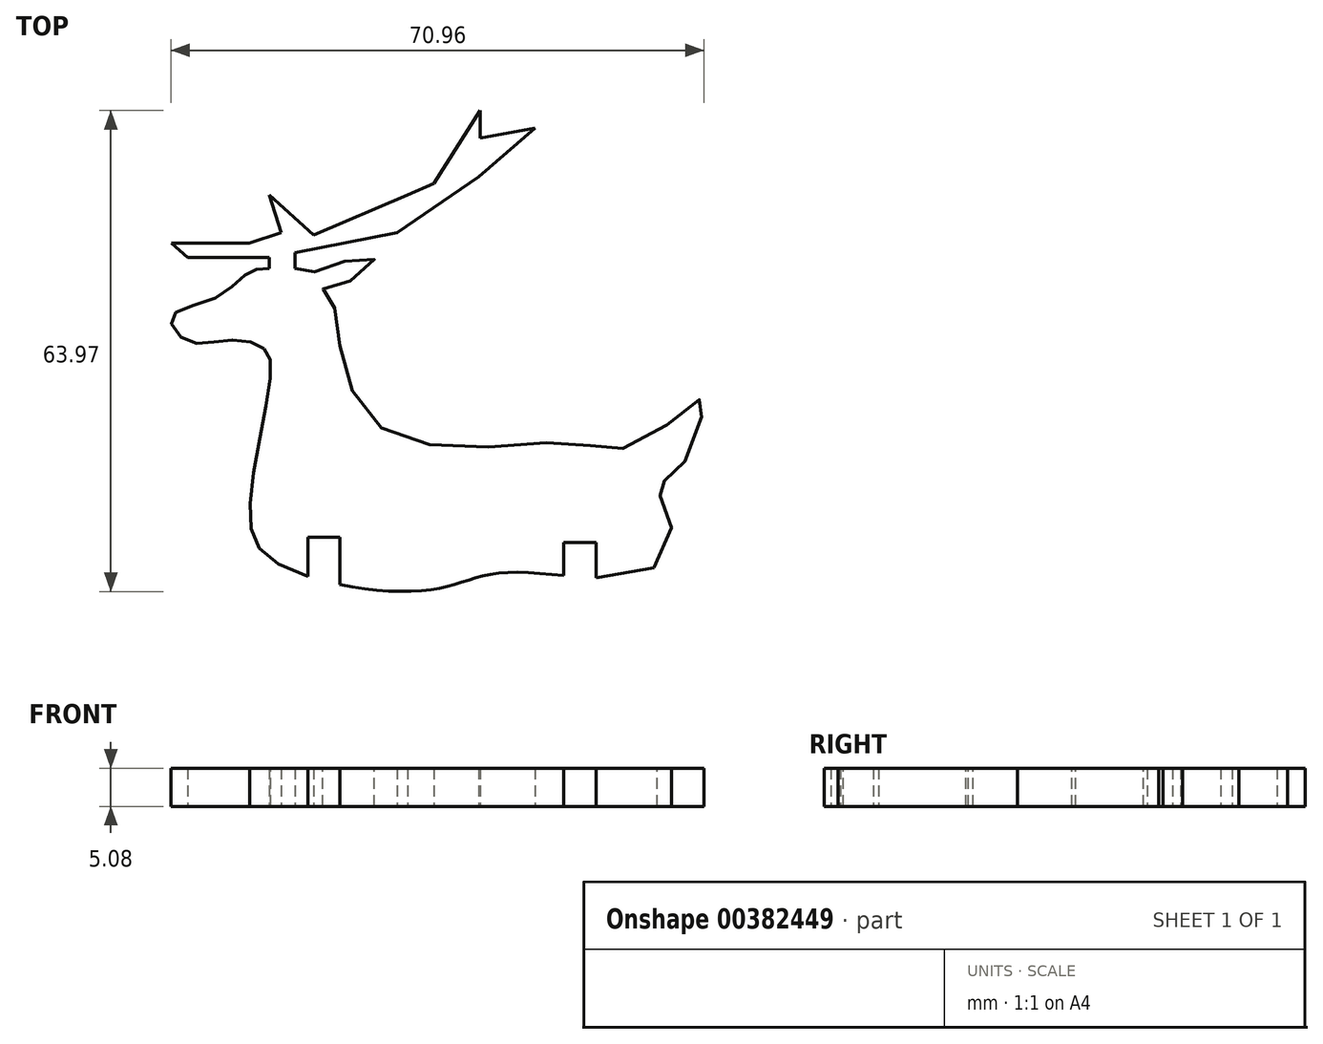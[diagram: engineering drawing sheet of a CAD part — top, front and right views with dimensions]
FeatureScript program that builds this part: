
annotation { "Feature Type Name" : "Feature", "Feature Type Description" : "" }
export const myFeature = defineFeature(function(context is Context, id is Id, definition is map)
    precondition{}
    {
        {
            var Q0;
            Q0=qCreatedBy(makeId("Top.planeOp"),FACE);
            var sketch = newSketch(context, id + "F0", { "sketchPlane" : qUnion([Q0])});
            skFitSpline(sketch, "E0", {"points": [v(-34.96, 24.7) * mm, v(-37.12, 27.92) * mm, v(-31.22, 30.47) * mm, v(-26.8, 33.87) * mm, v(-24.1, 34.38) * mm, v(-20.7, 34.38) * mm, v(-18.66, 33.87) * mm, v(-15.94, 34.72) * mm, v(-10.17, 35.74) * mm, v(-13.4, 32.68) * mm, v(-16.96, 31.66) * mm, v(-15.77, 29.96) * mm, v(-14.58, 23.34) * mm, v(-10, 13.83) * mm, v(3.08, 10.6) * mm, v(17.34, 11.11) * mm, v(22.78, 10.43) * mm, v(32.29, 16.2) * mm, v(33.7, 17.06) * mm, v(31.6, 9.42) * mm, v(28.55, 6.19) * mm, v(27.53, 5) * mm, v(28.89, 2.62) * mm, v(27.2, -5.36) * mm, v(7.5, -6.04) * mm, v(-3.03, -8.41) * mm, v(-23.58, -4.5) * mm, v(-26.64, 3.64) * mm, v(-23.92, 20.45) * mm, v(-24.94, 23.85) * mm, v(-29.7, 24.87) * mm, v(-34.96, 24.7) * mm]});
            skLineSegment(sketch, "E1", {"start": v(-24.1, 34.38) * mm, "end": v(-24.1, 35.84) * mm});
            skLineSegment(sketch, "E2", {"start": v(-24.1, 35.84) * mm, "end": v(-34.96, 35.84) * mm});
            skLineSegment(sketch, "E3", {"start": v(-34.96, 35.84) * mm, "end": v(-37.12, 37.77) * mm});
            skLineSegment(sketch, "E4", {"start": v(-37.12, 37.77) * mm, "end": v(-26.8, 37.77) * mm});
            skLineSegment(sketch, "E5", {"start": v(-26.8, 37.77) * mm, "end": v(-22.5, 39.15) * mm});
            skLineSegment(sketch, "E6", {"start": v(-22.5, 39.15) * mm, "end": v(-24.1, 44.16) * mm});
            skLineSegment(sketch, "E7", {"start": v(-24.1, 44.16) * mm, "end": v(-21.57, 41.9) * mm});
            skLineSegment(sketch, "E8", {"start": v(-21.57, 41.9) * mm, "end": v(-18.17, 38.86) * mm});
            skLineSegment(sketch, "E9", {"start": v(-18.17, 38.86) * mm, "end": v(-5.67, 44.16) * mm});
            skLineSegment(sketch, "E10", {"start": v(-5.67, 44.16) * mm, "end": v(-2.2, 45.7) * mm});
            skLineSegment(sketch, "E11", {"start": v(-2.2, 45.7) * mm, "end": v(3.93, 55.4) * mm});
            skLineSegment(sketch, "E12", {"start": v(3.93, 55.4) * mm, "end": v(3.93, 51.7) * mm});
            skLineSegment(sketch, "E13", {"start": v(3.93, 51.7) * mm, "end": v(11.23, 53.06) * mm});
            skLineSegment(sketch, "E14", {"start": v(11.23, 53.06) * mm, "end": v(3.76, 46.6) * mm});
            skLineSegment(sketch, "E15", {"start": v(3.76, 46.6) * mm, "end": v(-7.1, 39.13) * mm});
            skLineSegment(sketch, "E16", {"start": v(-7.1, 39.13) * mm, "end": v(-24.1, 35.84) * mm});
            skLineSegment(sketch, "E17", {"start": v(-20.7, 34.38) * mm, "end": v(-20.7, 36.5) * mm});
            skLineSegment(sketch, "E18.top", {"start": v(-18.96, -1.37) * mm, "end": v(-14.68, -1.37) * mm});
            skLineSegment(sketch, "E18.left", {"start": v(-18.96, -6.59) * mm, "end": v(-18.96, -1.37) * mm});
            skLineSegment(sketch, "E18.right", {"start": v(-14.68, -7.68) * mm, "end": v(-14.68, -1.37) * mm});
            skLineSegment(sketch, "E19.bottom", {"start": v(15.08, -2.07) * mm, "end": v(19.36, -2.07) * mm});
            skLineSegment(sketch, "E19.left", {"start": v(15.08, -2.07) * mm, "end": v(15.08, -6.44) * mm});
            skLineSegment(sketch, "E19.right", {"start": v(19.36, -2.07) * mm, "end": v(19.36, -6.73) * mm});
            skSolve(sketch);
        }
        {
            var Q0;
            {var subQ0=sQuery(id+"F0.wireOp",EDGE,"E0");var subQ1=makeQuery(id+"F0.imprint","INTERSECT",VERTEX,{"derivedFrom":[subQ0,sQuery(id+"F0.wireOp",EDGE,"E1")]});Q0=makeQuery(id+"F0.imprint","IMPRINT",FACE,{"disambiguationData":[TD([[makeQuery(id+"F0.imprint","IMPRINT",EDGE,{"disambiguationData":[TD([[subQ1,-1.0]])],"derivedFrom":subQ0}),-1.0]])]});}
            var Q1;
            {var subQ0=sQuery(id+"F0.wireOp",EDGE,"E1");Q1=makeQuery(id+"F0.imprint","IMPRINT",FACE,{"disambiguationData":[TD([[makeQuery(id+"F0.imprint","IMPRINT",EDGE,{"derivedFrom":subQ0}),-1.0]])]});}
            var Q2;
            {var subQ0=sQuery(id+"F0.wireOp",EDGE,"E2");Q2=makeQuery(id+"F0.imprint","IMPRINT",FACE,{"disambiguationData":[TD([[makeQuery(id+"F0.imprint","IMPRINT",EDGE,{"derivedFrom":subQ0}),-1.0]])]});}
            extrude(context, id + "F1", {"entities" : qUnion([Q0, Q1, Q2]), "depth" : 5.08 * mm});
        }
    });
